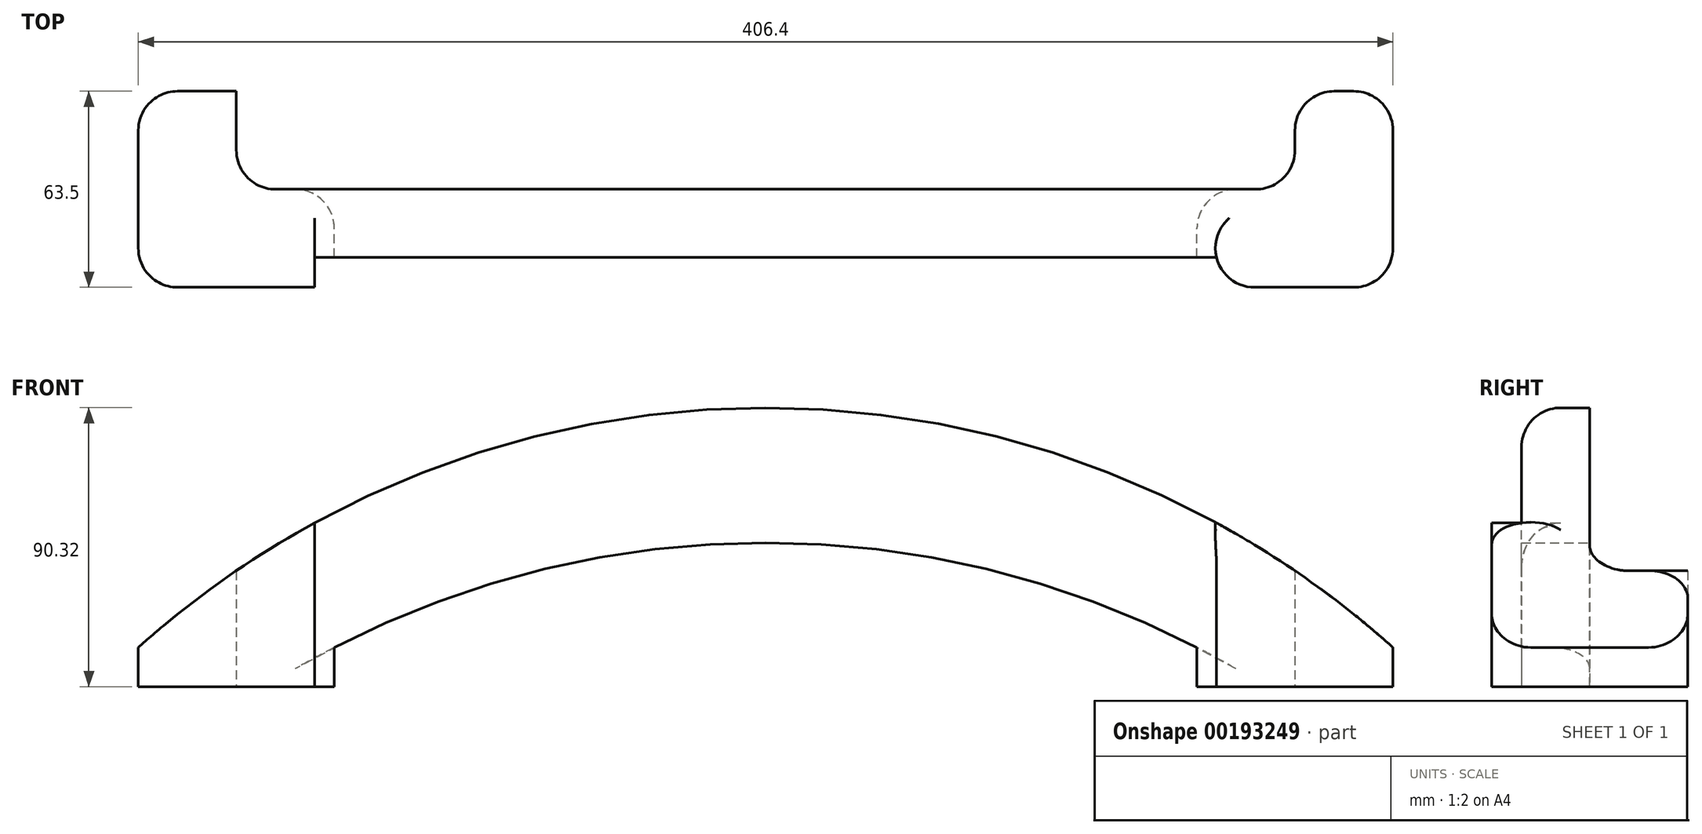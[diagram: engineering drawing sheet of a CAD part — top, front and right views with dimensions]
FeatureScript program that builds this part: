
annotation { "Feature Type Name" : "Feature", "Feature Type Description" : "" }
export const myFeature = defineFeature(function(context is Context, id is Id, definition is map)
    precondition{}
    {
        {
            var Q0;
            Q0=qCreatedBy(makeId("Front.planeOp"),FACE);
            var sketch = newSketch(context, id + "F0", { "sketchPlane" : qUnion([Q0])});
            skLineSegment(sketch, "E0", {"start": v(-203.2, 0) * mm, "end": v(203.2, 0) * mm, "construction": true});
            skArc(sketch, "E1", {"start": v(203.2, 0) * mm, "mid": v(0, 77.62) * mm, "end": v(-203.2, 0) * mm});
            skLineSegment(sketch, "E2", {"start": v(-203.2, 0) * mm, "end": v(-139.7, 0) * mm});
            skLineSegment(sketch, "E3", {"start": v(203.2, 0) * mm, "end": v(139.7, 0) * mm});
            skArc(sketch, "E4", {"start": v(139.7, 0) * mm, "mid": v(0, 33.9) * mm, "end": v(-139.7, 0) * mm});
            skSolve(sketch);
        }
        {
            var Q0;
            Q0 = qSketchRegion(id + "F0", true);
            extrude(context, id + "F1", {"entities" : qUnion([Q0]), "depth" : 63.5 * mm});
        }
        {
            var Q0;
            Q0=makeQuery(id+"F1.opExtrude","SWEPT_FACE",FACE,{"disambiguationData":[OSD([sQuery(id+"F0.wireOp",EDGE,"E2")])]});
            var Q1;
            Q1=makeQuery(id+"F1.opExtrude","SWEPT_FACE",FACE,{"disambiguationData":[OSD([sQuery(id+"F0.wireOp",EDGE,"E3")])]});
            extrude(context, id + "F2", {"entities" : qUnion([Q0, Q1]), "operationType" : NewBodyOperationType.ADD, "depth" : 12.7 * mm});
        }
        {
            var Q0;
            Q0=makeQuery(id+"F2.opExtrude","CAP_FACE",FACE,{"disambiguationData":[OSD([sQuery(id+"F0.wireOp",EDGE,"E2")])],"isStart":false});
            var sketch = newSketch(context, id + "F3", { "sketchPlane" : qUnion([Q0])});
            skLineSegment(sketch, "E5.bottom", {"start": v(146.05, 53.85) * mm, "end": v(-146.05, 53.85) * mm});
            skLineSegment(sketch, "E5.top", {"start": v(146.05, 57.15) * mm, "end": v(-146.05, 57.15) * mm, "construction": true});
            skLineSegment(sketch, "E5.left", {"start": v(146.05, 53.85) * mm, "end": v(146.05, 57.15) * mm});
            skLineSegment(sketch, "E5.right", {"start": v(-146.05, 53.85) * mm, "end": v(-146.05, 57.15) * mm});
            skPoint(sketch, "E5.middle", {"position": v(0, 55.5) * mm});
            skLineSegment(sketch, "E6", {"start": v(-146.05, 57.15) * mm, "end": v(-146.05, 63.5) * mm});
            skLineSegment(sketch, "E7", {"start": v(-146.05, 63.5) * mm, "end": v(146.05, 63.5) * mm});
            skLineSegment(sketch, "E8", {"start": v(146.05, 63.5) * mm, "end": v(146.05, 57.15) * mm});
            skSolve(sketch);
        }
        {
            var Q0;
            Q0 = qSketchRegion(id + "F3", true);
            extrude(context, id + "F4", {"entities" : qUnion([Q0]), "operationType" : NewBodyOperationType.REMOVE, "endBound" : BoundingType.THROUGH_ALL, "oppositeDirection" : true, "depth" : 25.4 * mm});
        }
        {
            var Q0;
            Q0=makeQuery(id+"F2.opExtrude","CAP_FACE",FACE,{"disambiguationData":[OSD([sQuery(id+"F0.wireOp",EDGE,"E2")])],"isStart":false});
            var sketch = newSketch(context, id + "F5", { "sketchPlane" : qUnion([Q0])});
            skLineSegment(sketch, "E9", {"start": v(-171.45, 0) * mm, "end": v(-171.45, 31.75) * mm});
            skPoint(sketch, "E9.endSnap0", {"position": v(-203.2, 31.75) * mm});
            skLineSegment(sketch, "E10", {"start": v(-171.45, 31.75) * mm, "end": v(-139.7, 31.75) * mm});
            skLineSegment(sketch, "E11", {"start": v(139.83, 31.75) * mm, "end": v(171.45, 31.75) * mm});
            skLineSegment(sketch, "E12", {"start": v(171.45, 31.75) * mm, "end": v(171.45, 0) * mm});
            skLineSegment(sketch, "E13", {"start": v(-139.7, 0) * mm, "end": v(-171.45, 0) * mm});
            skLineSegment(sketch, "E14", {"start": v(139.83, 0) * mm, "end": v(171.45, 0) * mm});
            skLineSegment(sketch, "E15", {"start": v(-139.7, 31.75) * mm, "end": v(139.83, 31.75) * mm});
            skLineSegment(sketch, "E16", {"start": v(139.83, 0) * mm, "end": v(-139.7, 0) * mm});
            skSolve(sketch);
        }
        {
            var Q0;
            Q0 = qSketchRegion(id + "F5", true);
            extrude(context, id + "F6", {"entities" : qUnion([Q0]), "operationType" : NewBodyOperationType.REMOVE, "endBound" : BoundingType.THROUGH_ALL, "oppositeDirection" : true, "depth" : 25.4 * mm});
        }
        {
            var Q0;
            Q0=makeQuery(id+"F6.boolean.opBoolean","COPY",EDGE,{"derivedFrom":makeQuery(id+"F6.opExtrude","SWEPT_EDGE",EDGE,{"disambiguationData":[OSD([sQuery(id+"F0.wireOp",EDGE,"E2"),sQuery(id+"F5.wireOp",EDGE,"E9"),sQuery(id+"F5.wireOp",EDGE,"E13")])]})});
            var Q1;
            Q1=makeQuery(id+"F6.boolean.opBoolean","COPY",EDGE,{"derivedFrom":makeQuery(id+"F6.opExtrude","SWEPT_EDGE",EDGE,{"disambiguationData":[OSD([sQuery(id+"F5.wireOp",EDGE,"E9"),sQuery(id+"F5.wireOp",EDGE,"E10")])]})});
            var Q2;
            Q2=makeQuery(id+"F6.boolean.opBoolean","INTERSECT",EDGE,{"derivedFrom":[makeQuery(id+"F2.opExtrude","SWEPT_FACE",FACE,{"disambiguationData":[OSD([sQuery(id+"F0.wireOp",EDGE,"E2"),sQuery(id+"F0.wireOp",EDGE,"E4")])]}),makeQuery(id+"F6.opExtrude","SWEPT_FACE",FACE,{"disambiguationData":[OSD([sQuery(id+"F5.wireOp",EDGE,"E10"),sQuery(id+"F5.wireOp",EDGE,"E11"),sQuery(id+"F5.wireOp",EDGE,"E15")])]})]});
            var Q3;
            Q3=makeQuery(id+"F6.boolean.opBoolean","COPY",EDGE,{"derivedFrom":makeQuery(id+"F6.opExtrude","SWEPT_EDGE",EDGE,{"disambiguationData":[OSD([sQuery(id+"F5.wireOp",EDGE,"E12"),sQuery(id+"F5.wireOp",EDGE,"E14")])]})});
            var Q4;
            Q4=makeQuery(id+"F6.boolean.opBoolean","COPY",EDGE,{"derivedFrom":makeQuery(id+"F6.opExtrude","SWEPT_EDGE",EDGE,{"disambiguationData":[OSD([sQuery(id+"F5.wireOp",EDGE,"E11"),sQuery(id+"F5.wireOp",EDGE,"E12")])]})});
            var Q5;
            {var subQ0=sQuery(id+"F0.wireOp",EDGE,"E3");var subQ1=sQuery(id+"F0.wireOp",EDGE,"E1");Q5=makeQuery(id+"F2.opExtrude","SWEPT_EDGE",EDGE,{"disambiguationData":[OSD([subQ1,subQ0]),TDD([makeQuery(id+"F1.opExtrude","CAP_VERTEX",VERTEX,{"disambiguationData":[OSD([subQ1,subQ0])],"isStart":true})])]});}
            var Q6;
            {var subQ0=sQuery(id+"F0.wireOp",EDGE,"E3");var subQ1=sQuery(id+"F0.wireOp",EDGE,"E1");Q6=makeQuery(id+"F2.opExtrude","SWEPT_EDGE",EDGE,{"disambiguationData":[OSD([subQ1,subQ0]),TDD([makeQuery(id+"F1.opExtrude","CAP_VERTEX",VERTEX,{"disambiguationData":[OSD([subQ1,subQ0])],"isStart":false})])]});}
            var Q7;
            Q7=makeQuery(id+"F4.boolean.opBoolean","COPY",EDGE,{"derivedFrom":makeQuery(id+"F4.opExtrude","SWEPT_EDGE",EDGE,{"disambiguationData":[OSD([sQuery(id+"F3.wireOp",EDGE,"E7"),sQuery(id+"F3.wireOp",EDGE,"E8")])]})});
            var Q8;
            Q8=makeQuery(id+"F4.boolean.opBoolean","COPY",EDGE,{"derivedFrom":makeQuery(id+"F4.opExtrude","SWEPT_EDGE",EDGE,{"disambiguationData":[OSD([sQuery(id+"F0.wireOp",EDGE,"E2"),sQuery(id+"F3.wireOp",EDGE,"E6"),sQuery(id+"F3.wireOp",EDGE,"E7")])]})});
            var Q9;
            {var subQ0=sQuery(id+"F0.wireOp",EDGE,"E2");var subQ1=sQuery(id+"F0.wireOp",EDGE,"E1");Q9=makeQuery(id+"F2.opExtrude","SWEPT_EDGE",EDGE,{"disambiguationData":[OSD([subQ1,subQ0]),TDD([makeQuery(id+"F1.opExtrude","CAP_VERTEX",VERTEX,{"disambiguationData":[OSD([subQ1,subQ0])],"isStart":false})])]});}
            var Q10;
            {var subQ0=sQuery(id+"F0.wireOp",EDGE,"E2");var subQ1=sQuery(id+"F0.wireOp",EDGE,"E1");Q10=makeQuery(id+"F2.opExtrude","SWEPT_EDGE",EDGE,{"disambiguationData":[OSD([subQ1,subQ0]),TDD([makeQuery(id+"F1.opExtrude","CAP_VERTEX",VERTEX,{"disambiguationData":[OSD([subQ1,subQ0])],"isStart":true})])]});}
            var Q11;
            Q11=makeQuery(id+"F6.boolean.opBoolean","INTERSECT",EDGE,{"derivedFrom":[makeQuery(id+"F2.opExtrude","SWEPT_FACE",FACE,{"disambiguationData":[OSD([sQuery(id+"F0.wireOp",EDGE,"E3"),sQuery(id+"F0.wireOp",EDGE,"E4")])]}),makeQuery(id+"F6.opExtrude","SWEPT_FACE",FACE,{"disambiguationData":[OSD([sQuery(id+"F5.wireOp",EDGE,"E10"),sQuery(id+"F5.wireOp",EDGE,"E11"),sQuery(id+"F5.wireOp",EDGE,"E15")])]})]});
            fillet(context, id + "F7", {"entities" : qUnion([Q0, Q1, Q2, Q3, Q4, Q5, Q6, Q7, Q8, Q9, Q10, Q11]), "radius" : 12.7 * mm, "tangentPropagation" : true, "allowEdgeOverflow" : false});
        }
        {
            var Q0;
            Q0=makeQuery(id+"F4.boolean.opBoolean","INTERSECT",EDGE,{"derivedFrom":[makeQuery(id+"F1.opExtrude","SWEPT_FACE",FACE,{"disambiguationData":[OSD([sQuery(id+"F0.wireOp",EDGE,"E1")])]}),makeQuery(id+"F4.opExtrude","SWEPT_FACE",FACE,{"disambiguationData":[OSD([sQuery(id+"F3.wireOp",EDGE,"E5.bottom")])]})]});
            fillet(context, id + "F8", {"entities" : qUnion([Q0]), "radius" : 12.7 * mm, "tangentPropagation" : true, "allowEdgeOverflow" : false});
        }
    });
